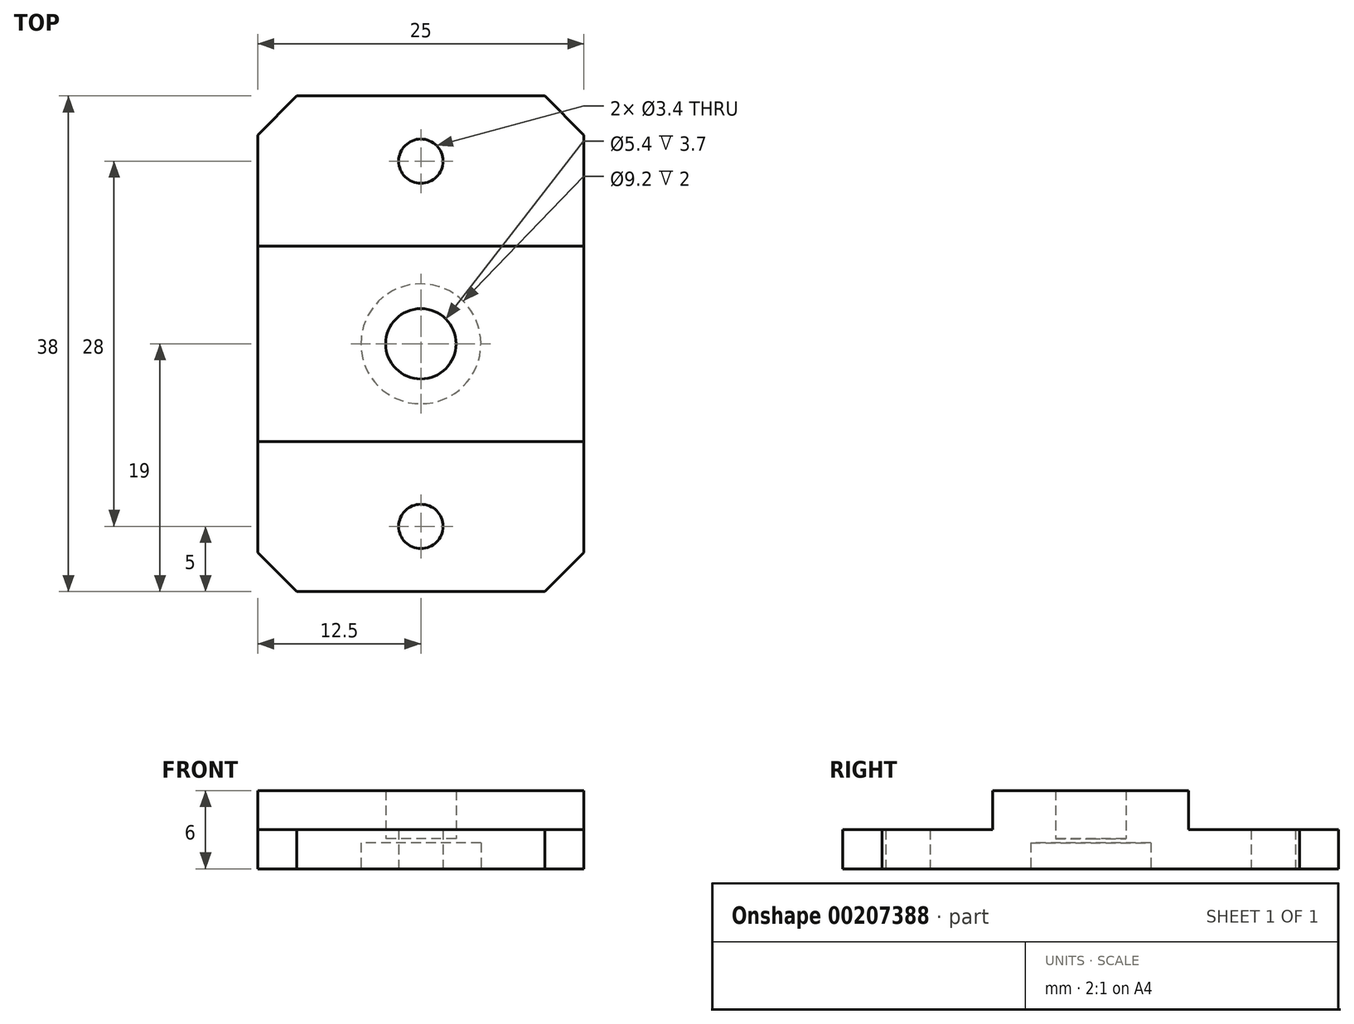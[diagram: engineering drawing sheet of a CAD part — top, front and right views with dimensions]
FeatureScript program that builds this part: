
annotation { "Feature Type Name" : "Feature", "Feature Type Description" : "" }
export const myFeature = defineFeature(function(context is Context, id is Id, definition is map)
    precondition{}
    {
        {
            var Q0;
            Q0=qCreatedBy(makeId("Top.planeOp"),FACE);
            var sketch = newSketch(context, id + "F0", { "sketchPlane" : qUnion([Q0])});
            skLineSegment(sketch, "E0.bottom", {"start": v(-12.5, 19) * mm, "end": v(12.5, 19) * mm});
            skLineSegment(sketch, "E0.top", {"start": v(-12.5, -19) * mm, "end": v(12.5, -19) * mm});
            skCircle(sketch, "E1", {"center": v(0, 14) * mm, "radius": 1.7 * mm});
            skCircle(sketch, "E2", {"center": v(0, -14) * mm, "radius": 1.7 * mm});
            skPoint(sketch, "E3", {"position": v(0, 19) * mm});
            skPoint(sketch, "E4.rect.middle", {"position": v(0, 0) * mm});
            skCircle(sketch, "E5", {"center": v(0, 0) * mm, "radius": 2.7 * mm});
            skCircle(sketch, "E6", {"center": v(0, 0) * mm, "radius": 4.6 * mm});
            skLineSegment(sketch, "E7", {"start": v(-12.5, 19) * mm, "end": v(-12.5, -19) * mm});
            skLineSegment(sketch, "E8", {"start": v(12.5, -19) * mm, "end": v(12.5, 19) * mm});
            skLineSegment(sketch, "E9", {"start": v(-12.5, 7.5) * mm, "end": v(12.5, 7.5) * mm});
            skLineSegment(sketch, "E10", {"start": v(-12.5, -7.5) * mm, "end": v(12.5, -7.5) * mm});
            skPoint(sketch, "E11", {"position": v(12.5, 0) * mm});
            skLineSegment(sketch, "E12", {"start": v(5.33, 7.5) * mm, "end": v(5.33, -7.5) * mm, "construction": true});
            skPoint(sketch, "E13", {"position": v(5.33, 0) * mm});
            skLineSegment(sketch, "E14", {"start": v(0, 14) * mm, "end": v(0, 14) * mm});
            skSolve(sketch);
        }
        {
            var Q0;
            Q0=makeQuery(id+"F0.imprint","IMPRINT",FACE,{"disambiguationData":[TD([[makeQuery(id+"F0.imprint","IMPRINT",EDGE,{"derivedFrom":sQuery(id+"F0.wireOp",EDGE,"E0.bottom")}),-1.0]])]});
            var Q1;
            {var subQ1=sQuery(id+"F0.wireOp",EDGE,"E0.top");Q1=makeQuery(id+"F0.imprint","IMPRINT",FACE,{"disambiguationData":[TD([[makeQuery(id+"F0.imprint","IMPRINT",EDGE,{"derivedFrom":subQ1}),1.0]])]});}
            extrude(context, id + "F1", {"entities" : qUnion([Q0, Q1]), "depth" : 3 * mm});
        }
        {
            var Q0;
            Q0=makeQuery(id+"F0.imprint","IMPRINT",FACE,{"disambiguationData":[TD([[makeQuery(id+"F0.imprint","IMPRINT",EDGE,{"derivedFrom":sQuery(id+"F0.wireOp",EDGE,"E6")}),-1.0]])]});
            var Q1;
            Q1=makeQuery(id+"F0.imprint","IMPRINT",FACE,{"disambiguationData":[TD([[makeQuery(id+"F0.imprint","IMPRINT",EDGE,{"derivedFrom":sQuery(id+"F0.wireOp",EDGE,"E5")}),-1.0]])]});
            extrude(context, id + "F2", {"entities" : qUnion([Q0, Q1]), "operationType" : NewBodyOperationType.ADD, "depth" : 6 * mm});
        }
        {
            var Q0;
            Q0=makeQuery(id+"F0.imprint","IMPRINT",FACE,{"disambiguationData":[TD([[makeQuery(id+"F0.imprint","IMPRINT",EDGE,{"derivedFrom":sQuery(id+"F0.wireOp",EDGE,"E5")}),-1.0]])]});
            extrude(context, id + "F3", {"entities" : qUnion([Q0]), "operationType" : NewBodyOperationType.REMOVE, "depth" : 2 * mm});
        }
        {
            var Q0;
            Q0=makeQuery(id+"F1.opExtrude","CAP_EDGE",EDGE,{"disambiguationData":[OSD([sQuery(id+"F0.wireOp",EDGE,"E9")])],"isStart":false});
            var Q1;
            Q1=makeQuery(id+"F1.opExtrude","CAP_EDGE",EDGE,{"disambiguationData":[OSD([sQuery(id+"F0.wireOp",EDGE,"E10")])],"isStart":false});
            var Q2;
            Q2=makeQuery(id+"F1.opExtrude","SWEPT_EDGE",EDGE,{"disambiguationData":[OSD([sQuery(id+"F0.wireOp",EDGE,"E0.top"),sQuery(id+"F0.wireOp",EDGE,"E8")])]});
            var Q3;
            Q3=makeQuery(id+"F1.opExtrude","SWEPT_EDGE",EDGE,{"disambiguationData":[OSD([sQuery(id+"F0.wireOp",EDGE,"E0.top"),sQuery(id+"F0.wireOp",EDGE,"E7")])]});
            var Q4;
            Q4=makeQuery(id+"F1.opExtrude","SWEPT_EDGE",EDGE,{"disambiguationData":[OSD([sQuery(id+"F0.wireOp",EDGE,"E0.bottom"),sQuery(id+"F0.wireOp",EDGE,"E8")])]});
            var Q5;
            Q5=makeQuery(id+"F1.opExtrude","SWEPT_EDGE",EDGE,{"disambiguationData":[OSD([sQuery(id+"F0.wireOp",EDGE,"E0.bottom"),sQuery(id+"F0.wireOp",EDGE,"E7")])]});
            chamfer(context, id + "F4", {"entities" : qUnion([Q0, Q1, Q2, Q3, Q4, Q5]), "width" : 3 * mm, "tangentPropagation" : true});
        }
        {
            var Q0;
            Q0=makeQuery(id+"F0.imprint","IMPRINT",FACE,{"disambiguationData":[TD([[makeQuery(id+"F0.imprint","IMPRINT",EDGE,{"derivedFrom":sQuery(id+"F0.wireOp",EDGE,"E5")}),1.0]])]});
            extrude(context, id + "F5", {"entities" : qUnion([Q0]), "operationType" : NewBodyOperationType.ADD, "depth" : 2.3 * mm, "hasSecondDirection" : true, "secondDirectionOppositeDirection" : false, "secondDirectionDepth" : 2 * mm});
        }
    });
